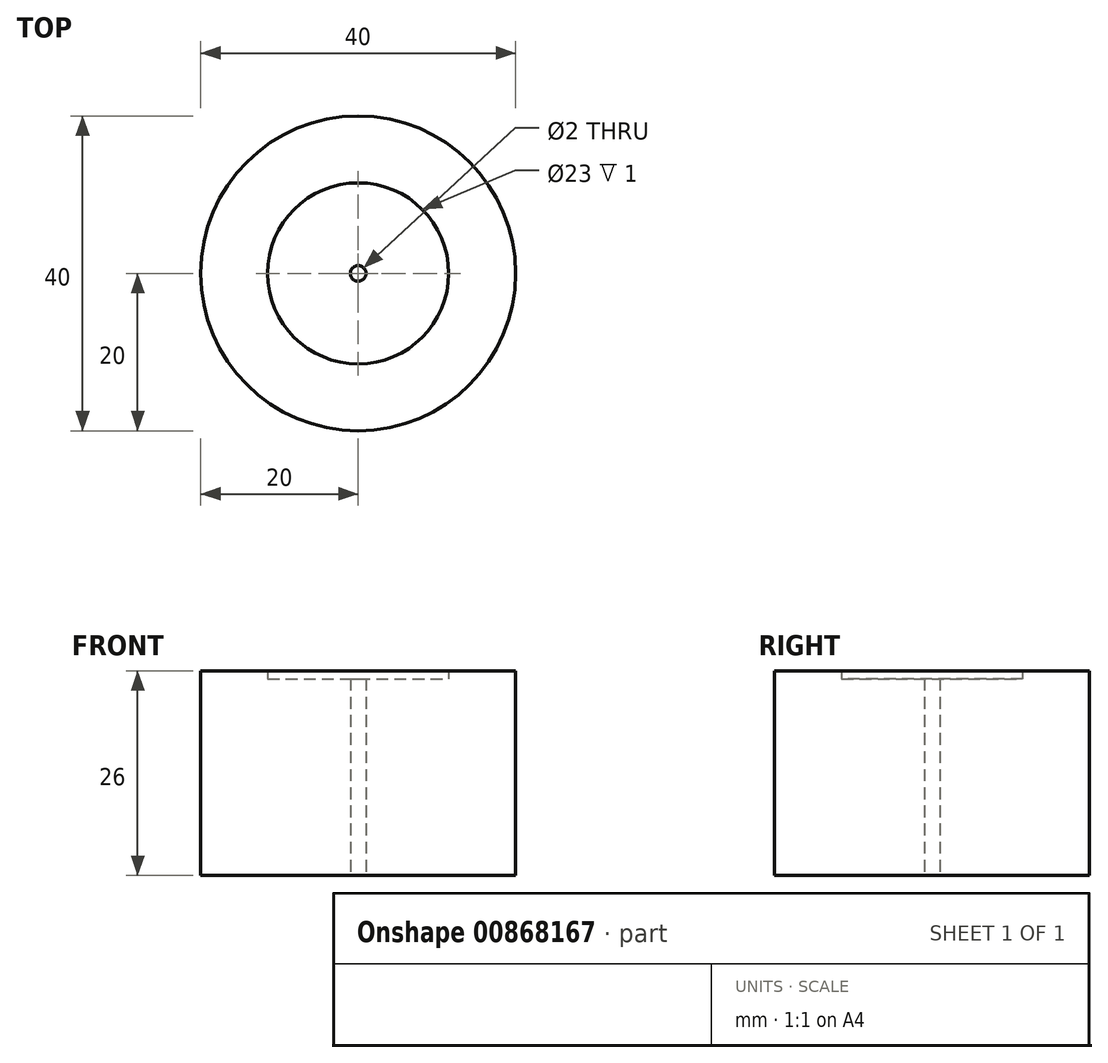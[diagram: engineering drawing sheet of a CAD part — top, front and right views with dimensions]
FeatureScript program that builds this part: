
annotation { "Feature Type Name" : "Feature", "Feature Type Description" : "" }
export const myFeature = defineFeature(function(context is Context, id is Id, definition is map)
    precondition{}
    {
        {
            var Q0;
            Q0=qCreatedBy(makeId("Top.planeOp"),FACE);
            var sketch = newSketch(context, id + "F0", { "sketchPlane" : qUnion([Q0])});
            skCircle(sketch, "E0", {"center": v(0, 0) * mm, "radius": 20 * mm});
            skSolve(sketch);
        }
        {
            var Q0;
            Q0 = qSketchRegion(id + "F0", true);
            extrude(context, id + "F1", {"entities" : qUnion([Q0]), "depth" : 25 * mm, "offsetDistance" : 25.4 * mm});
        }
        {
            var Q0;
            Q0=sQuery(id+"F0.wireOp",VERTEX,"E0.center");
            var Q1;
            Q1=makeQuery(id+"F1.opExtrude","SWEPT_BODY",BODY,{"disambiguationData":[OSD([sQuery(id+"F0.wireOp",EDGE,"E0")])]});
            hole(context, id + "F2", {"style" : HoleStyle.SIMPLE, "endStyle" : HoleEndStyle.BLIND, "oppositeDirection" : true, "holeDiameter" : 2 * mm, "majorDiameter" : 5 * mm, "holeDepth" : 27 * mm, "isTappedThrough" : true, "tappedDepth" : 12 * mm, "tapClearance" : 3, "locations" : qUnion([Q0]), "scope" : qUnion([Q1])});
        }
        {
            var Q0;
            Q0=makeQuery(id+"F1.opExtrude","CAP_FACE",FACE,{"disambiguationData":[OSD([sQuery(id+"F0.wireOp",EDGE,"E0")])],"isStart":false});
            var sketch = newSketch(context, id + "F3", { "sketchPlane" : qUnion([Q0])});
            skCircle(sketch, "E1", {"center": v(0, 0) * mm, "radius": 20 * mm});
            skSolve(sketch);
        }
        {
            var Q0;
            Q0 = qSketchRegion(id + "F3", true);
            extrude(context, id + "F4", {"entities" : qUnion([Q0]), "operationType" : NewBodyOperationType.ADD, "depth" : 1 * mm, "offsetDistance" : 25 * mm});
        }
        {
            var Q0;
            Q0=sQuery(id+"F3.wireOp",VERTEX,"E1.center");
            var Q1;
            Q1=makeQuery(id+"F1.opExtrude","SWEPT_BODY",BODY,{"disambiguationData":[OSD([sQuery(id+"F0.wireOp",EDGE,"E0")])]});
            hole(context, id + "F5", {"style" : HoleStyle.SIMPLE, "endStyle" : HoleEndStyle.BLIND, "oppositeDirection" : true, "holeDiameter" : 23 * mm, "majorDiameter" : 5 * mm, "holeDepth" : 4 * mm, "isTappedThrough" : true, "tappedDepth" : 12 * mm, "tapClearance" : 3, "locations" : qUnion([Q0]), "scope" : qUnion([Q1])});
        }
    });
